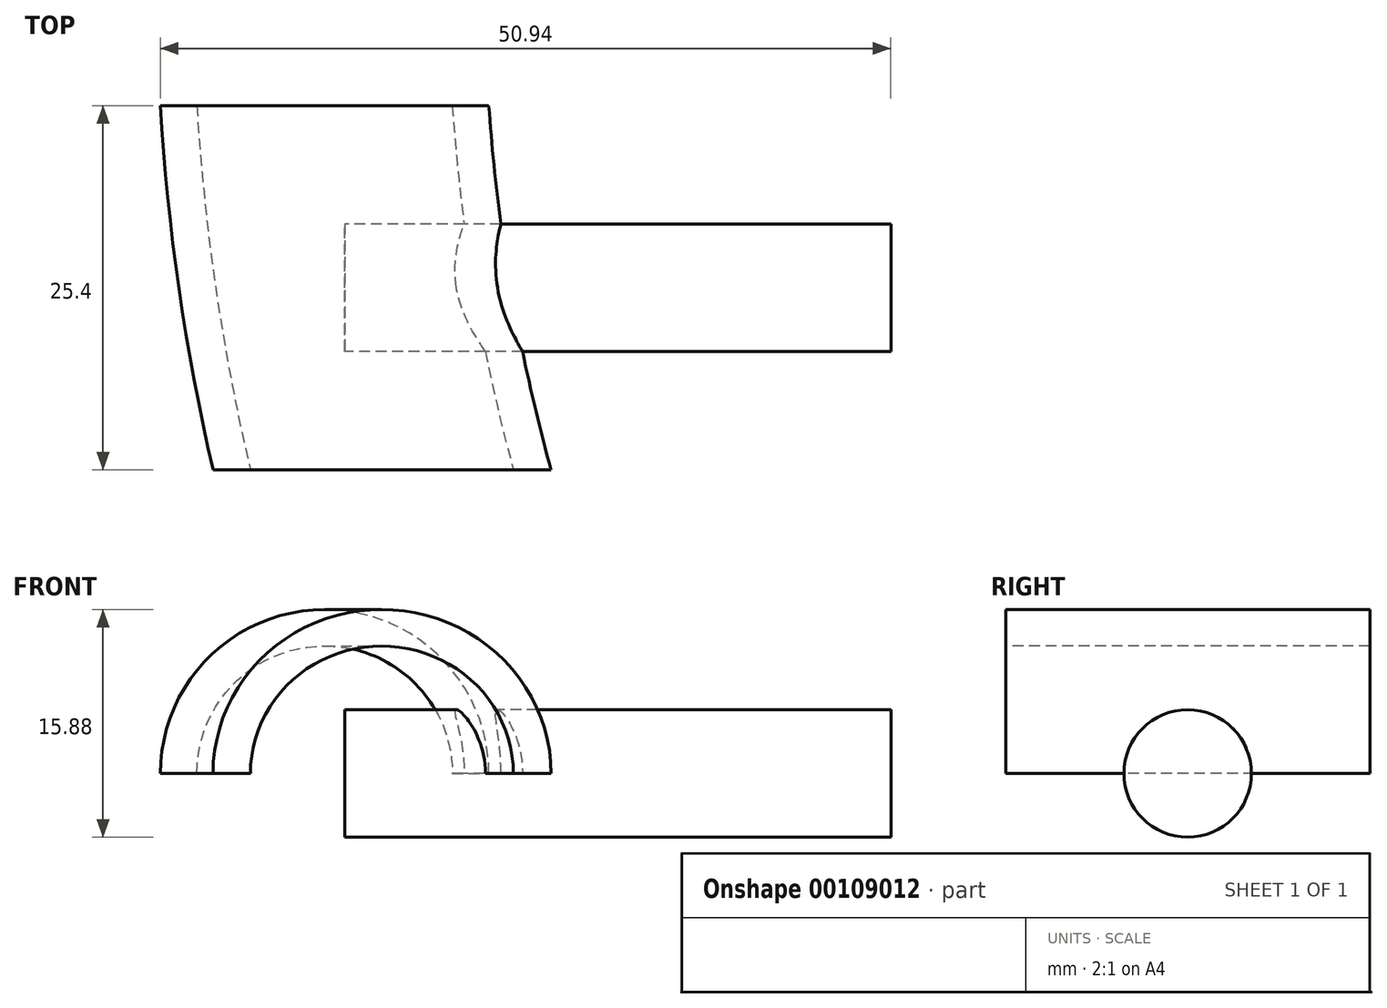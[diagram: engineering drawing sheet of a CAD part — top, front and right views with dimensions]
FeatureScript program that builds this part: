
annotation { "Feature Type Name" : "Feature", "Feature Type Description" : "" }
export const myFeature = defineFeature(function(context is Context, id is Id, definition is map)
    precondition{}
    {
        {
            var Q0;
            Q0=qCreatedBy(makeId("Top.planeOp"),FACE);
            var sketch = newSketch(context, id + "F0", { "sketchPlane" : qUnion([Q0])});
            skCircle(sketch, "E0", {"center": v(0, 0) * mm, "radius": 132.08 * mm});
            skLineSegment(sketch, "E1", {"start": v(0, 0) * mm, "end": v(94.44, 0) * mm});
            skLineSegment(sketch, "E2", {"start": v(94.44, 0) * mm, "end": v(94.44, -21.72) * mm});
            skLineSegment(sketch, "E3", {"start": v(94.44, -21.72) * mm, "end": v(-130.28, -21.72) * mm});
            skLineSegment(sketch, "E4", {"start": v(-130.28, -21.72) * mm, "end": v(-139.29, -21.72) * mm});
            skLineSegment(sketch, "E5", {"start": v(94.44, 0) * mm, "end": v(140.97, 0) * mm});
            skArc(sketch, "E6", {"start": v(140.97, 0) * mm, "mid": v(-140.96, 1.57) * mm, "end": v(140.93, -3.15) * mm});
            skArc(sketch, "E7", {"start": v(140.93, -3.15) * mm, "mid": v(140.96, -1.57) * mm, "end": v(140.97, 0) * mm});
            skLineSegment(sketch, "E8", {"start": v(-83.36, -21.72) * mm, "end": v(-83.36, -34.42) * mm});
            skLineSegment(sketch, "E9", {"start": v(-83.36, -34.42) * mm, "end": v(-198.69, -34.42) * mm});
            skLineSegment(sketch, "E10", {"start": v(-198.69, -34.42) * mm, "end": v(-198.69, -9.02) * mm});
            skLineSegment(sketch, "E11", {"start": v(-198.69, -9.02) * mm, "end": v(-83.36, -9.02) * mm});
            skLineSegment(sketch, "E12", {"start": v(-83.36, -21.72) * mm, "end": v(-83.36, -9.02) * mm});
            skLineSegment(sketch, "E13", {"start": v(-181.88, -9.02) * mm, "end": v(-181.88, 166.5) * mm});
            skLineSegment(sketch, "E14", {"start": v(-181.88, 166.5) * mm, "end": v(186.07, 166.5) * mm});
            skLineSegment(sketch, "E15", {"start": v(186.07, 166.5) * mm, "end": v(186.07, -162.28) * mm});
            skLineSegment(sketch, "E16", {"start": v(186.07, -162.28) * mm, "end": v(-181.88, -162.28) * mm});
            skLineSegment(sketch, "E17", {"start": v(-181.88, -162.28) * mm, "end": v(-181.88, -34.42) * mm});
            skLineSegment(sketch, "E18", {"start": v(94.44, -16) * mm, "end": v(-83.36, -16) * mm});
            skSolve(sketch);
        }
        {
            var Q0;
            Q0=sQuery(id+"F0.wireOp",EDGE,"E6");
            var Q1;
            Q1=sQuery(id+"F0.wireOp",VERTEX,"E7.end");
            cPlane(context, id + "F1", {"entities" : qUnion([Q0, Q1]), "cplaneType" : CPlaneType.CURVE_POINT, "offset" : 25.4 * mm, "width" : 152.4 * mm, "height" : 152.4 * mm});
        }
        {
            var Q0;
            Q0=qCreatedBy(id+"F1.planeOp",FACE);
            var sketch = newSketch(context, id + "F2", { "sketchPlane" : qUnion([Q0])});
            skCircle(sketch, "E19", {"center": v(-140.97, 0) * mm, "radius": 11.43 * mm});
            skCircle(sketch, "E20", {"center": v(-140.97, 0) * mm, "radius": 8.9 * mm});
            skSolve(sketch);
        }
        {
            var Q0;
            Q0=makeQuery(id+"F2.imprint","IMPRINT",FACE,{"disambiguationData":[TD([[makeQuery(id+"F2.imprint","IMPRINT",EDGE,{"derivedFrom":sQuery(id+"F2.wireOp",EDGE,"E19")}),1.0]])]});
            var Q1;
            Q1=sQuery(id+"F0.wireOp",EDGE,"E6");
            var Q2;
            Q2=sQuery(id+"F0.wireOp",EDGE,"E7");
            sweep(context, id + "F3", {"profiles" : qUnion([Q0]), "path" : qUnion([Q1, Q2])});
        }
        {
            var Q0;
            {var subQ4=sQuery(id+"F0.wireOp",EDGE,"E7");Q0=makeQuery(id+"F0.imprint","IMPRINT",FACE,{"disambiguationData":[TD([[makeQuery(id+"F0.imprint","IMPRINT",EDGE,{"derivedFrom":subQ4}),-1.0]])]});}
            var Q1;
            {var subQ1=sQuery(id+"F0.wireOp",EDGE,"E2");Q1=makeQuery(id+"F0.imprint","IMPRINT",FACE,{"disambiguationData":[TD([[makeQuery(id+"F0.imprint","IMPRINT",EDGE,{"derivedFrom":subQ1}),1.0]])]});}
            var Q2;
            {var subQ1=sQuery(id+"F0.wireOp",EDGE,"E2");Q2=makeQuery(id+"F0.imprint","IMPRINT",FACE,{"disambiguationData":[TD([[makeQuery(id+"F0.imprint","IMPRINT",EDGE,{"derivedFrom":subQ1}),-1.0]])]});}
            var Q3;
            {var subQ0=sQuery(id+"F0.wireOp",EDGE,"E7");Q3=makeQuery(id+"F0.imprint","IMPRINT",FACE,{"disambiguationData":[TD([[makeQuery(id+"F0.imprint","IMPRINT",EDGE,{"derivedFrom":subQ0}),1.0]])]});}
            var Q4;
            {var subQ0=sQuery(id+"F0.wireOp",EDGE,"E11");var subQ1=sQuery(id+"F0.wireOp",EDGE,"E0");var subQ2=makeQuery(id+"F0.imprint","INTERSECT",VERTEX,{"derivedFrom":[subQ1,subQ0]});Q4=makeQuery(id+"F0.imprint","IMPRINT",FACE,{"disambiguationData":[TD([[makeQuery(id+"F0.imprint","IMPRINT",EDGE,{"disambiguationData":[TD([[subQ2,1.0]])],"derivedFrom":subQ1}),-1.0]])]});}
            var Q5;
            {var subQ9=sQuery(id+"F0.wireOp",EDGE,"E18");Q5=makeQuery(id+"F0.imprint","IMPRINT",FACE,{"disambiguationData":[TD([[makeQuery(id+"F0.imprint","IMPRINT",EDGE,{"derivedFrom":subQ9}),-1.0]])]});}
            extrude(context, id + "F4", {"entities" : qUnion([Q0, Q1, Q2, Q3, Q4, Q5]), "operationType" : NewBodyOperationType.REMOVE, "depth" : 25.4 * mm, "hasSecondDirection" : true, "secondDirectionOppositeDirection" : true, "secondDirectionDepth" : 25.4 * mm});
        }
        {
            var Q0;
            {var subQ0=sQuery(id+"F0.wireOp",EDGE,"E10");Q0=makeQuery(id+"F0.imprint","IMPRINT",FACE,{"disambiguationData":[TD([[makeQuery(id+"F0.imprint","IMPRINT",EDGE,{"derivedFrom":subQ0}),-1.0]])]});}
            var Q1;
            {var subQ5=sQuery(id+"F0.wireOp",EDGE,"E12");Q1=makeQuery(id+"F0.imprint","IMPRINT",FACE,{"disambiguationData":[TD([[makeQuery(id+"F0.imprint","IMPRINT",EDGE,{"derivedFrom":subQ5}),1.0]])]});}
            var Q2;
            {var subQ5=sQuery(id+"F0.wireOp",EDGE,"E8");Q2=makeQuery(id+"F0.imprint","IMPRINT",FACE,{"disambiguationData":[TD([[makeQuery(id+"F0.imprint","IMPRINT",EDGE,{"derivedFrom":subQ5}),-1.0]])]});}
            var Q3;
            {var subQ0=sQuery(id+"F0.wireOp",EDGE,"E4");Q3=makeQuery(id+"F0.imprint","IMPRINT",FACE,{"disambiguationData":[TD([[makeQuery(id+"F0.imprint","IMPRINT",EDGE,{"derivedFrom":subQ0}),1.0]])]});}
            var Q4;
            {var subQ0=sQuery(id+"F0.wireOp",EDGE,"E4");Q4=makeQuery(id+"F0.imprint","IMPRINT",FACE,{"disambiguationData":[TD([[makeQuery(id+"F0.imprint","IMPRINT",EDGE,{"derivedFrom":subQ0}),-1.0]])]});}
            extrude(context, id + "F5", {"entities" : qUnion([Q0, Q1, Q2, Q3, Q4]), "operationType" : NewBodyOperationType.REMOVE, "oppositeDirection" : true, "depth" : 25.4 * mm});
        }
        {
            var Q0;
            Q0=sQuery(id+"F0.wireOp",EDGE,"E4");
            var Q1;
            Q1=sQuery(id+"F0.wireOp",VERTEX,"E4.end");
            cPlane(context, id + "F6", {"entities" : qUnion([Q0, Q1]), "cplaneType" : CPlaneType.LINE_POINT, "offset" : 25.4 * mm, "width" : 152.4 * mm, "height" : 152.4 * mm});
        }
        {
            var Q0;
            Q0=qCreatedBy(id+"F6.planeOp",FACE);
            var sketch = newSketch(context, id + "F7", { "sketchPlane" : qUnion([Q0])});
            skCircle(sketch, "E21", {"center": v(21.72, 0) * mm, "radius": 4.45 * mm});
            skSolve(sketch);
        }
        {
            var Q0;
            Q0=makeQuery(id+"F7.imprint","IMPRINT",FACE,{"disambiguationData":[TD([[makeQuery(id+"F7.imprint","IMPRINT",EDGE,{"derivedFrom":sQuery(id+"F7.wireOp",EDGE,"E21")}),1.0]])]});
            extrude(context, id + "F8", {"entities" : qUnion([Q0]), "operationType" : NewBodyOperationType.ADD, "oppositeDirection" : true, "depth" : 38.1 * mm});
        }
    });
